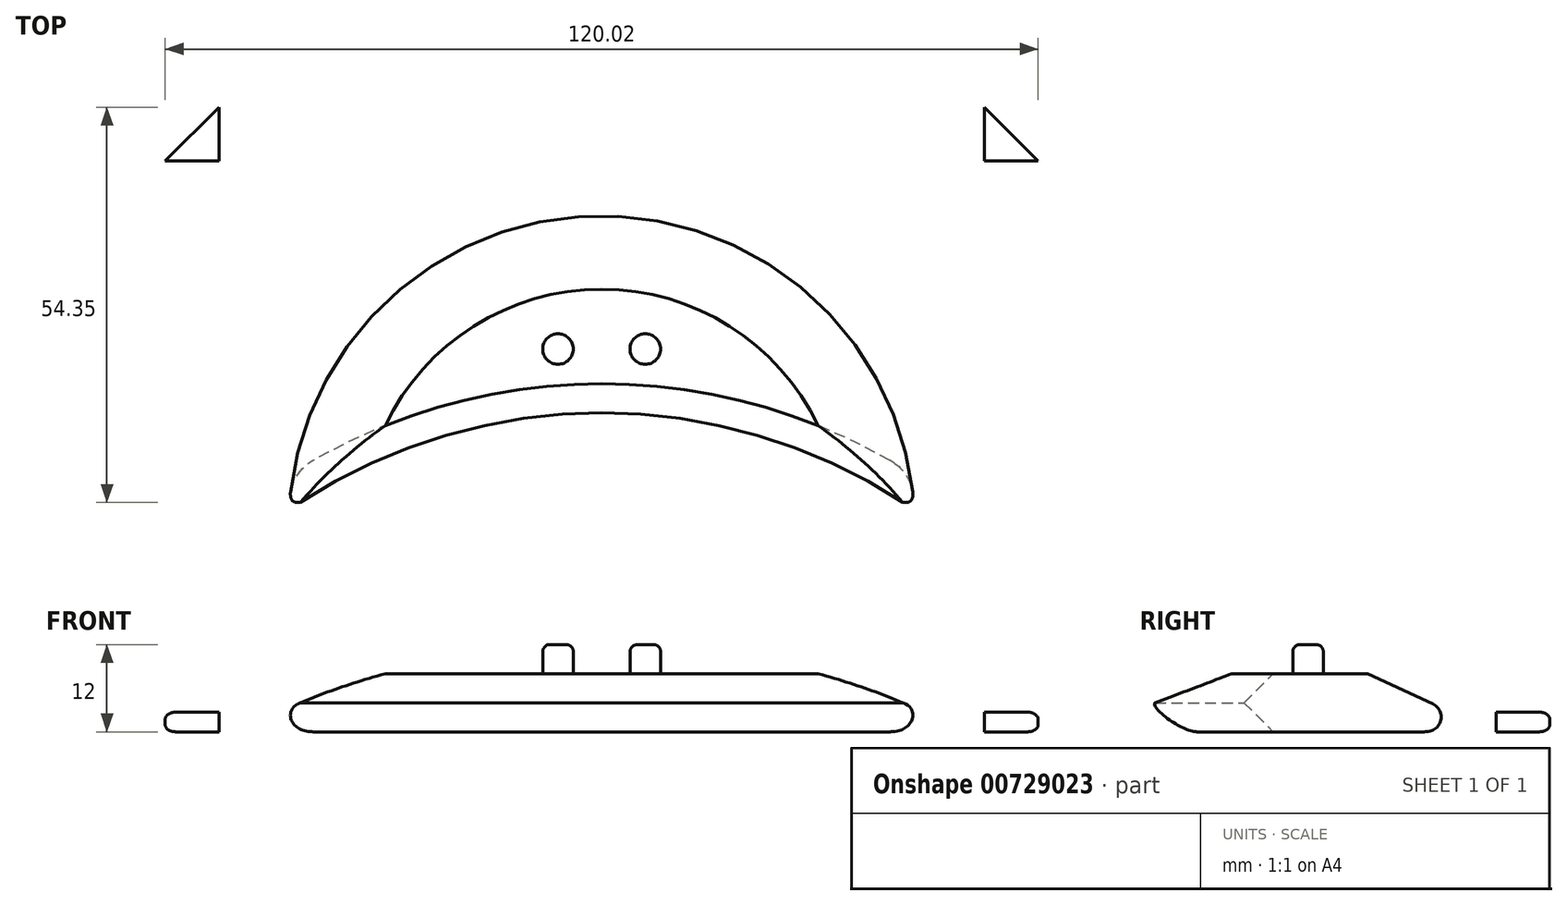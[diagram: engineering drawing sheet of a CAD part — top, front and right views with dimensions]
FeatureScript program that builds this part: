
annotation { "Feature Type Name" : "Feature", "Feature Type Description" : "" }
export const myFeature = defineFeature(function(context is Context, id is Id, definition is map)
    precondition{}
    {
        {
            var Q0;
            Q0=qCreatedBy(makeId("Top.planeOp"),FACE);
            var sketch = newSketch(context, id + "F0", { "sketchPlane" : qUnion([Q0])});
            skLineSegment(sketch, "E0", {"start": v(45, 0) * mm, "end": v(-45, 0) * mm, "construction": true});
            skLineSegment(sketch, "E1", {"start": v(0, 0) * mm, "end": v(0, 30) * mm, "construction": true});
            skLineSegment(sketch, "E2", {"start": v(-45, 0) * mm, "end": v(-45, -15) * mm, "construction": true});
            skLineSegment(sketch, "E3", {"start": v(45, 0) * mm, "end": v(45, -15) * mm, "construction": true});
            skCircle(sketch, "E4", {"center": v(0, -15) * mm, "radius": 45 * mm});
            skCircle(sketch, "E5", {"center": v(0, -75) * mm, "radius": 75 * mm});
            skSolve(sketch);
        }
        {
            var Q0;
            {var subQ0=sQuery(id+"F0.wireOp",EDGE,"E5");var subQ1=sQuery(id+"F0.wireOp",EDGE,"E4");var subQ2=makeQuery(id+"F0.imprint","INTERSECT",VERTEX,{"disambiguationData":[OD(0.0)],"derivedFrom":[subQ1,subQ0]});Q0=makeQuery(id+"F0.imprint","IMPRINT",FACE,{"disambiguationData":[TD([[makeQuery(id+"F0.imprint","IMPRINT",EDGE,{"disambiguationData":[TD([[subQ2,1.0]])],"derivedFrom":subQ1}),1.0]])]});}
            extrude(context, id + "F1", {"entities" : qUnion([Q0]), "depth" : 8 * mm, "offsetDistance" : 25 * mm});
        }
        {
            var Q0;
            Q0=makeQuery(id+"F1.opExtrude","CAP_EDGE",EDGE,{"disambiguationData":[OSD([sQuery(id+"F0.wireOp",EDGE,"E4")])],"isStart":false});
            chamfer(context, id + "F2", {"entities" : qUnion([Q0]), "chamferType" : ChamferType.OFFSET_ANGLE, "width" : 12 * mm, "oppositeDirection" : false, "angle" : 25 * degree, "tangentPropagation" : true});
        }
        {
            var Q0;
            Q0=makeQuery(id+"F1.opExtrude","CAP_EDGE",EDGE,{"disambiguationData":[OSD([sQuery(id+"F0.wireOp",EDGE,"E4")])],"isStart":true});
            fillet(context, id + "F3", {"entities" : qUnion([Q0]), "radius" : 5 * mm, "tangentPropagation" : true, "allowEdgeOverflow" : false});
        }
        {
            var Q0;
            Q0=makeQuery(id+"F1.opExtrude","CAP_EDGE",EDGE,{"disambiguationData":[OSD([sQuery(id+"F0.wireOp",EDGE,"E5")])],"isStart":false});
            var Q1;
            Q1=makeQuery(id+"F1.opExtrude","CAP_EDGE",EDGE,{"disambiguationData":[OSD([sQuery(id+"F0.wireOp",EDGE,"E5")])],"isStart":true});
            chamfer(context, id + "F4", {"entities" : qUnion([Q0, Q1]), "width" : 5 * mm, "tangentPropagation" : true});
        }
        {
            var Q0;
            {var subQ0=sQuery(id+"F0.wireOp",EDGE,"E4");Q0=makeQuery(id+"F3.opFillet","BLEND_EDGE",EDGE,{"blendedFrom":[makeQuery(id+"F1.opExtrude","CAP_EDGE",EDGE,{"disambiguationData":[OSD([subQ0])],"isStart":true}),makeQuery(id+"F2.opChamfer","BLEND_FACE",FACE,{"disambiguationData":[OSD([subQ0])]})],"blendedInto":[makeQuery(id+"F2.opChamfer","BLEND_FACE",FACE,{"disambiguationData":[OSD([subQ0])]})]});}
            fillet(context, id + "F5", {"entities" : qUnion([Q0]), "radius" : 2 * mm, "tangentPropagation" : true, "allowEdgeOverflow" : false});
        }
        {
            var Q0;
            Q0=makeQuery(id+"F1.opExtrude","CAP_FACE",FACE,{"disambiguationData":[OSD([sQuery(id+"F0.wireOp",EDGE,"E4"),sQuery(id+"F0.wireOp",EDGE,"E5")])],"isStart":false});
            var sketch = newSketch(context, id + "F6", { "sketchPlane" : qUnion([Q0])});
            skLineSegment(sketch, "E6", {"start": v(0, 9.79) * mm, "end": v(6, 9.79) * mm, "construction": true});
            skLineSegment(sketch, "E7", {"start": v(6, 9.79) * mm, "end": v(-6, 9.79) * mm, "construction": true});
            skCircle(sketch, "E8", {"center": v(-6, 9.79) * mm, "radius": 2.1 * mm});
            skCircle(sketch, "E9", {"center": v(6, 9.79) * mm, "radius": 2.1 * mm});
            skSolve(sketch);
        }
        {
            var Q0;
            Q0=makeQuery(id+"F6.imprint","IMPRINT",FACE,{"disambiguationData":[TD([[makeQuery(id+"F6.imprint","IMPRINT",EDGE,{"derivedFrom":sQuery(id+"F6.wireOp",EDGE,"E8")}),1.0]])]});
            var Q1;
            Q1=makeQuery(id+"F6.imprint","IMPRINT",FACE,{"disambiguationData":[TD([[makeQuery(id+"F6.imprint","IMPRINT",EDGE,{"derivedFrom":sQuery(id+"F6.wireOp",EDGE,"E9")}),1.0]])]});
            extrude(context, id + "F7", {"entities" : qUnion([Q0, Q1]), "operationType" : NewBodyOperationType.ADD, "depth" : 4 * mm, "offsetDistance" : 25 * mm});
        }
        {
            var Q0;
            Q0=makeQuery(id+"F7.opExtrude","CAP_EDGE",EDGE,{"disambiguationData":[OSD([sQuery(id+"F6.wireOp",EDGE,"E8")])],"isStart":false});
            var Q1;
            Q1=makeQuery(id+"F7.opExtrude","CAP_EDGE",EDGE,{"disambiguationData":[OSD([sQuery(id+"F6.wireOp",EDGE,"E9")])],"isStart":false});
            fillet(context, id + "F8", {"entities" : qUnion([Q0, Q1]), "radius" : 1 * mm, "tangentPropagation" : true, "allowEdgeOverflow" : false});
        }
        {
            var Q0;
            Q0=qCreatedBy(makeId("Top.planeOp"),FACE);
            var sketch = newSketch(context, id + "F9", { "sketchPlane" : qUnion([Q0])});
            skLineSegment(sketch, "E10", {"start": v(-60.01, 35.65) * mm, "end": v(-52.6, 43.03) * mm});
            skLineSegment(sketch, "E11", {"start": v(-52.6, 43.03) * mm, "end": v(-52.6, 35.65) * mm});
            skLineSegment(sketch, "E12", {"start": v(-52.6, 35.65) * mm, "end": v(-60.01, 35.65) * mm});
            skSolve(sketch);
        }
        {
            var Q0;
            Q0 = qSketchRegion(id + "F9", true);
            var Q1;
            Q1=makeQuery(id+"F9.imprint","IMPRINT",FACE,{"disambiguationData":[TD([[makeQuery(id+"F9.imprint","IMPRINT",EDGE,{"derivedFrom":sQuery(id+"F9.wireOp",EDGE,"E10")}),-1.0]])]});
            extrude(context, id + "F10", {"entities" : qUnion([Q0, Q1]), "depth" : 2.7 * mm, "offsetDistance" : 25 * mm});
        }
        {
            var Q0;
            Q0=makeQuery(id+"F10.opExtrude","CAP_EDGE",EDGE,{"disambiguationData":[OSD([sQuery(id+"F9.wireOp",EDGE,"E10")])],"isStart":false});
            var Q1;
            Q1=makeQuery(id+"F10.opExtrude","CAP_EDGE",EDGE,{"disambiguationData":[OSD([sQuery(id+"F9.wireOp",EDGE,"E10")])],"isStart":true});
            fillet(context, id + "F11", {"entities" : qUnion([Q0, Q1]), "radius" : 1 * mm, "tangentPropagation" : true, "allowEdgeOverflow" : false});
        }
        {
            var Q0;
            Q0=makeQuery(id+"F10.opExtrude","SWEPT_BODY",BODY,{"disambiguationData":[OSD([sQuery(id+"F9.wireOp",EDGE,"E10"),sQuery(id+"F9.wireOp",EDGE,"E11"),sQuery(id+"F9.wireOp",EDGE,"E12")])]});
            var Q1;
            Q1=qCreatedBy(makeId("Right.planeOp"),FACE);
            mirror(context, id + "F12", {"operationType" : NewBodyOperationType.ADD, "entities" : qUnion([Q0]), "mirrorPlane" : qUnion([Q1])});
        }
    });
